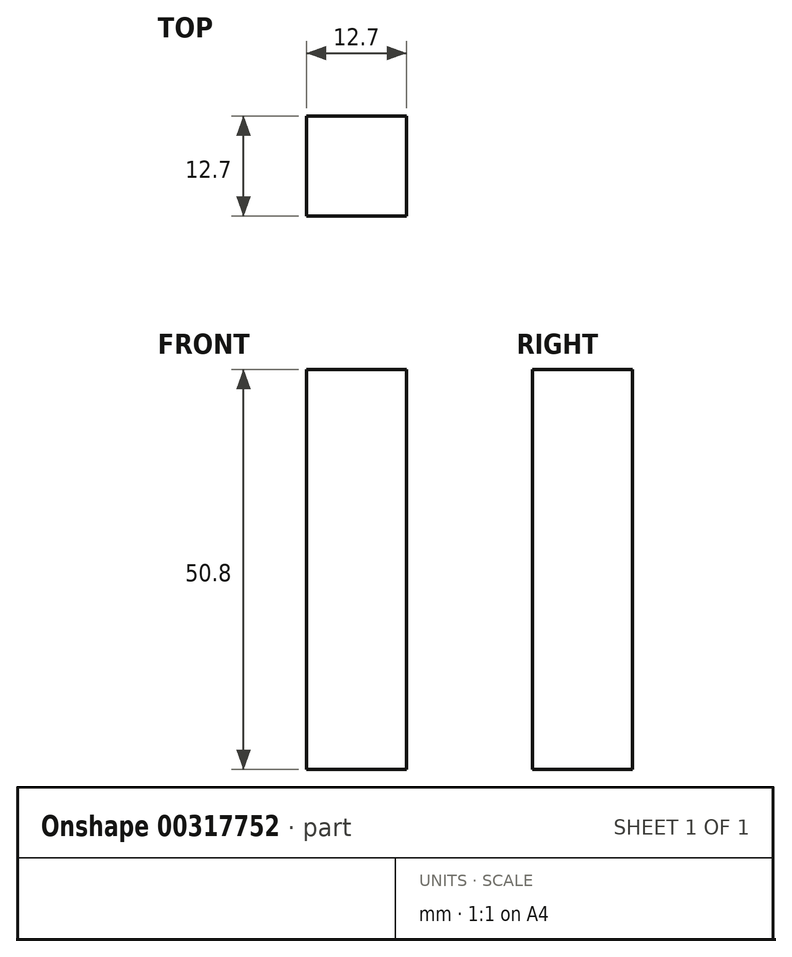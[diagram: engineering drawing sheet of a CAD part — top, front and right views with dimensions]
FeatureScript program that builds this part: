
annotation { "Feature Type Name" : "Feature", "Feature Type Description" : "" }
export const myFeature = defineFeature(function(context is Context, id is Id, definition is map)
    precondition{}
    {
        {
            var Q0;
            Q0=qCreatedBy(makeId("Top.planeOp"),FACE);
            var sketch = newSketch(context, id + "F0", { "sketchPlane" : qUnion([Q0])});
            skLineSegment(sketch, "E0.bottom", {"start": v(0, 0) * mm, "end": v(50.8, 0) * mm});
            skLineSegment(sketch, "E0.top", {"start": v(0, 50.8) * mm, "end": v(50.8, 50.8) * mm});
            skLineSegment(sketch, "E0.left", {"start": v(0, 0) * mm, "end": v(0, 50.8) * mm});
            skLineSegment(sketch, "E0.right", {"start": v(50.8, 0) * mm, "end": v(50.8, 50.8) * mm});
            skLineSegment(sketch, "E1.bottom", {"start": v(0, 50.8) * mm, "end": v(12.7, 50.8) * mm});
            skLineSegment(sketch, "E1.top", {"start": v(0, 38.1) * mm, "end": v(12.7, 38.1) * mm});
            skLineSegment(sketch, "E1.left", {"start": v(0, 50.8) * mm, "end": v(0, 38.1) * mm});
            skLineSegment(sketch, "E1.right", {"start": v(12.7, 50.8) * mm, "end": v(12.7, 38.1) * mm});
            skLineSegment(sketch, "E2.bottom", {"start": v(0, 0) * mm, "end": v(12.7, 0) * mm});
            skLineSegment(sketch, "E2.top", {"start": v(0, 12.7) * mm, "end": v(12.7, 12.7) * mm});
            skLineSegment(sketch, "E2.left", {"start": v(0, 0) * mm, "end": v(0, 12.7) * mm});
            skLineSegment(sketch, "E2.right", {"start": v(12.7, 0) * mm, "end": v(12.7, 12.7) * mm});
            skLineSegment(sketch, "E3.bottom", {"start": v(50.8, 12.7) * mm, "end": v(31.75, 12.7) * mm});
            skLineSegment(sketch, "E3.top", {"start": v(50.8, 38.1) * mm, "end": v(31.75, 38.1) * mm});
            skLineSegment(sketch, "E3.left", {"start": v(50.8, 12.7) * mm, "end": v(50.8, 38.1) * mm});
            skLineSegment(sketch, "E3.right", {"start": v(31.75, 12.7) * mm, "end": v(31.75, 38.1) * mm});
            skSolve(sketch);
        }
        {
            var Q0;
            {var subQ4=sQuery(id+"F0.wireOp",EDGE,"E0.bottom");Q0=makeQuery(id+"F0.imprint","IMPRINT",FACE,{"disambiguationData":[TD([[makeQuery(id+"F0.imprint","IMPRINT",EDGE,{"derivedFrom":subQ4}),1.0]])]});}
            extrude(context, id + "F1", {"entities" : qUnion([Q0]), "depth" : 50.8 * mm});
        }
        {
            var Q0;
            Q0=makeQuery(id+"F1.opExtrude","SWEPT_FACE",FACE,{"disambiguationData":[OSD([sQuery(id+"F0.wireOp",EDGE,"E0.bottom")])]});
            var sketch = newSketch(context, id + "F2", { "sketchPlane" : qUnion([Q0])});
            skLineSegment(sketch, "E4", {"start": v(25.4, 50.8) * mm, "end": v(50.8, 25.4) * mm});
            skLineSegment(sketch, "E5", {"start": v(50.8, 25.4) * mm, "end": v(50.8, 50.8) * mm});
            skLineSegment(sketch, "E6", {"start": v(50.8, 50.8) * mm, "end": v(25.4, 50.8) * mm});
            skSolve(sketch);
        }
        {
            var Q0;
            Q0 = qSketchRegion(id + "F2", true);
            extrude(context, id + "F3", {"entities" : qUnion([Q0]), "operationType" : NewBodyOperationType.REMOVE, "endBound" : BoundingType.THROUGH_ALL, "oppositeDirection" : true, "depth" : 25.4 * mm});
        }
    });
